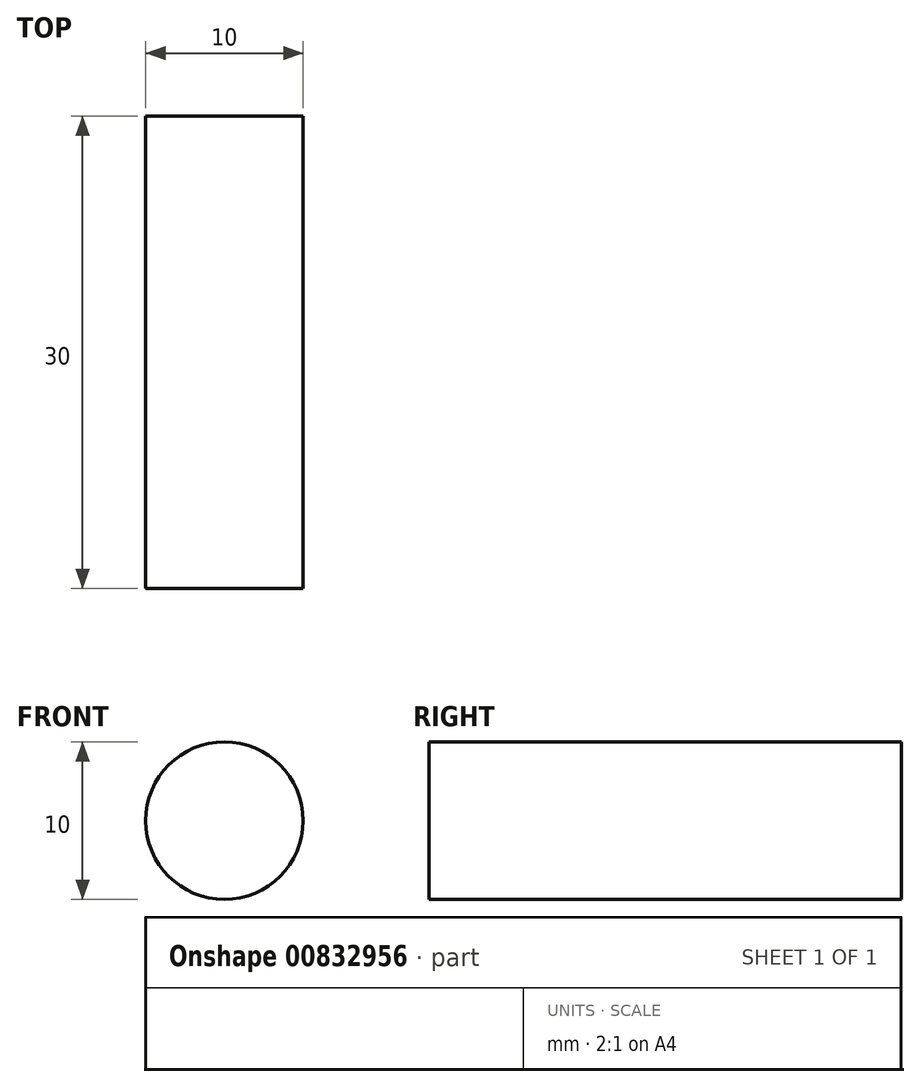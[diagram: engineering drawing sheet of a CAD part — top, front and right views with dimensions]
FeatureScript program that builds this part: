
annotation { "Feature Type Name" : "Feature", "Feature Type Description" : "" }
export const myFeature = defineFeature(function(context is Context, id is Id, definition is map)
    precondition{}
    {
        {
            var Q0;
            Q0=qCreatedBy(makeId("Front.planeOp"),FACE);
            var sketch = newSketch(context, id + "F0", { "sketchPlane" : qUnion([Q0])});
            skPoint(sketch, "E0.third.point", {"position": v(77.43, -43.66) * mm});
            skCircle(sketch, "E1", {"center": v(62.84, 12.63) * mm, "radius": 5 * mm});
            skSolve(sketch);
        }
        {
            var Q0;
            Q0=makeQuery(id+"F0.imprint","IMPRINT",FACE,{"disambiguationData":[TD([[makeQuery(id+"F0.imprint","IMPRINT",EDGE,{"derivedFrom":sQuery(id+"F0.wireOp",EDGE,"E1")}),1.0]])]});
            extrude(context, id + "F1", {"entities" : qUnion([Q0]), "depth" : 30 * mm, "offsetDistance" : 25 * mm});
        }
    });
